# Revit family: FS_Скамейка_Линия трехлучевая_R16
name_source: partatom
category: Антураж
revit_build: Autodesk Revit 2016 (Build: 20160314_0715(x64)
units: mm (PartAtom-declared; Revit-internal decimal feet)

## family parameters
Всегда вертикально = Да
Источник визуального образа = Геометрия семейства
На основе рабочей плоскости = Нет
Общий = Нет
При загрузке вырезать с полостями = Нет
Точка расчета площади = Нет

## types (1)
- Скамейка «Линия трехлучевая»
    ADSK_Код изделия = 12777
    ADSK_Материал доски = FS_Древесина
    ADSK_Материал крепления = FS_Цинк
    ADSK_Материал опоры = FS_Сталь
    ADSK_Наименование = Скамейка «Линия трехлучевая»
    ADSK_Размер_Высота = 440 мм
    ADSK_Размер_Длина = 3788 мм
    ADSK_Размер_Ширина = 530 мм
    URL = https://hobbyka.ru
    Высота = 0 мм
    Изготовитель = ООО 'Хоббика'
    Комментарии к типоразмеру = Материал: сталь, брус
    Стоимость = 148790 $

## geometry (parser evidence)
native form markers: Sweep x6
no freeform markers — native parametric forms only
